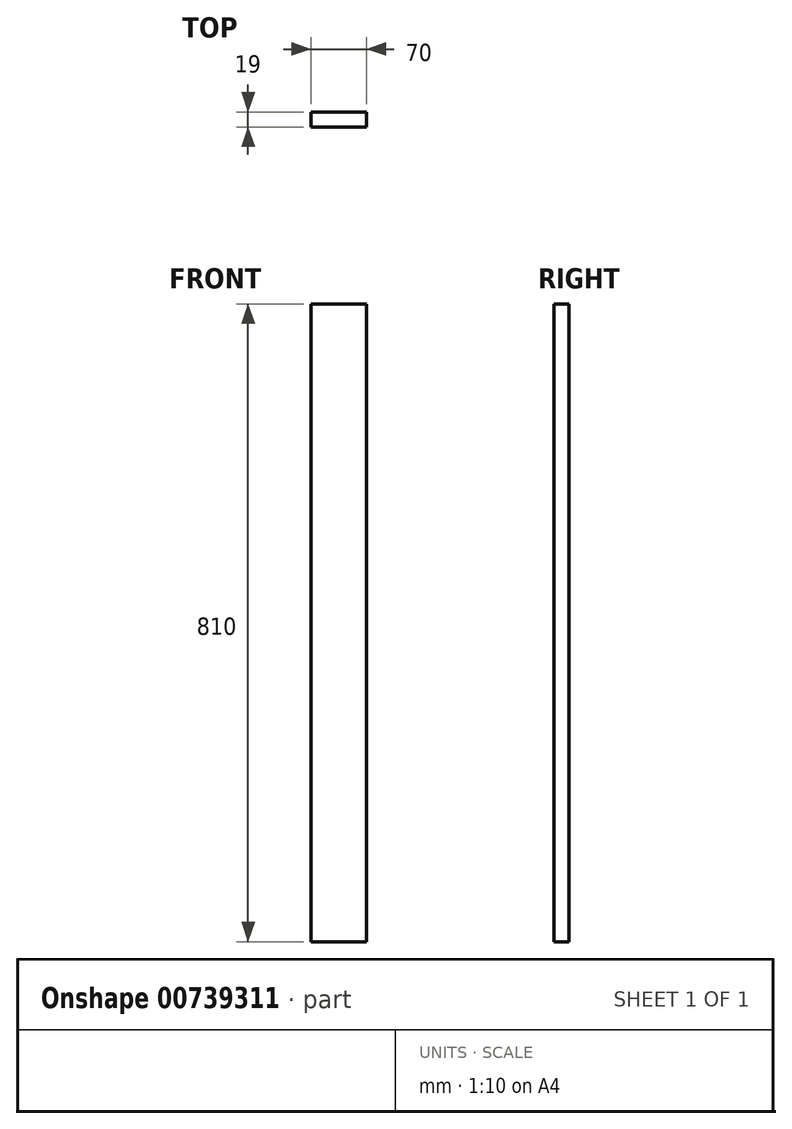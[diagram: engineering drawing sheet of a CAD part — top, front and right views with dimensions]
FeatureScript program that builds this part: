
annotation { "Feature Type Name" : "Feature", "Feature Type Description" : "" }
export const myFeature = defineFeature(function(context is Context, id is Id, definition is map)
    precondition{}
    {
        {
            var Q0;
            Q0=qCreatedBy(makeId("Top.planeOp"),FACE);
            var sketch = newSketch(context, id + "F0", { "sketchPlane" : qUnion([Q0])});
            skLineSegment(sketch, "E0.bottom", {"start": v(35, 9.5) * mm, "end": v(-35, 9.5) * mm});
            skLineSegment(sketch, "E0.top", {"start": v(35, -9.5) * mm, "end": v(-35, -9.5) * mm});
            skLineSegment(sketch, "E0.left", {"start": v(35, 9.5) * mm, "end": v(35, -9.5) * mm});
            skLineSegment(sketch, "E0.right", {"start": v(-35, 9.5) * mm, "end": v(-35, -9.5) * mm});
            skPoint(sketch, "E0.middle", {"position": v(0, 0) * mm});
            skSolve(sketch);
        }
        {
            var Q0;
            Q0=makeQuery(id+"F0.imprint","IMPRINT",FACE,{"disambiguationData":[TD([[makeQuery(id+"F0.imprint","IMPRINT",EDGE,{"derivedFrom":sQuery(id+"F0.wireOp",EDGE,"E0.bottom")}),1.0]])]});
            extrude(context, id + "F1", {"entities" : qUnion([Q0]), "depth" : 810 * mm, "offsetDistance" : 25 * mm});
        }
    });
